# Revit family: Stainless_Steel_Clothes_Hook-B-233
name_source: partatom
category: Plumbing Fixtures
revit_build: Autodesk Revit 2014 (Build: 20130308_1515(x64)
units: mm (PartAtom-declared; Revit-internal decimal feet)

## types (1)
- B-233
    ADA Compliant = Yes
    Assembly Code = C1030200
    CW Connection = No
    CWFU = 0
    Default Elevation = 45"
    Description = 11‑gauge (3.2mm), type 304 stainless steel, satin finish. Hook is 1 1⁄4" x 1 1⁄4" (30 x 30mm) and projects 1 1⁄8" (30mm) from wall. Unit is 2 1⁄4" (55mm) high
    HW Connection = No
    HWFU = 0
    Height = 1 1/8"
    Installation Type = Wall mounted
    Length = 2 1/4"
    Manufacturer = Bobrick
    Material = Stainless Steel, Satin Finish
    Model = B-233
    Price = Prices may vary. Please consult Manufacturer Representative for most up-to-date price list.
    Product Documentation Link = http://bobrick.com
    Product Page URL = http://bobrick.com
    URL = http://bobrick.com
    Vent Connection = No
    WFU = 0
    Warranty Information = 15 Years Warranty
    Waste Connection = No
    Width = 7/8"

## geometry (parser evidence)
native form markers: Sweep x3
no freeform markers — native parametric forms only
